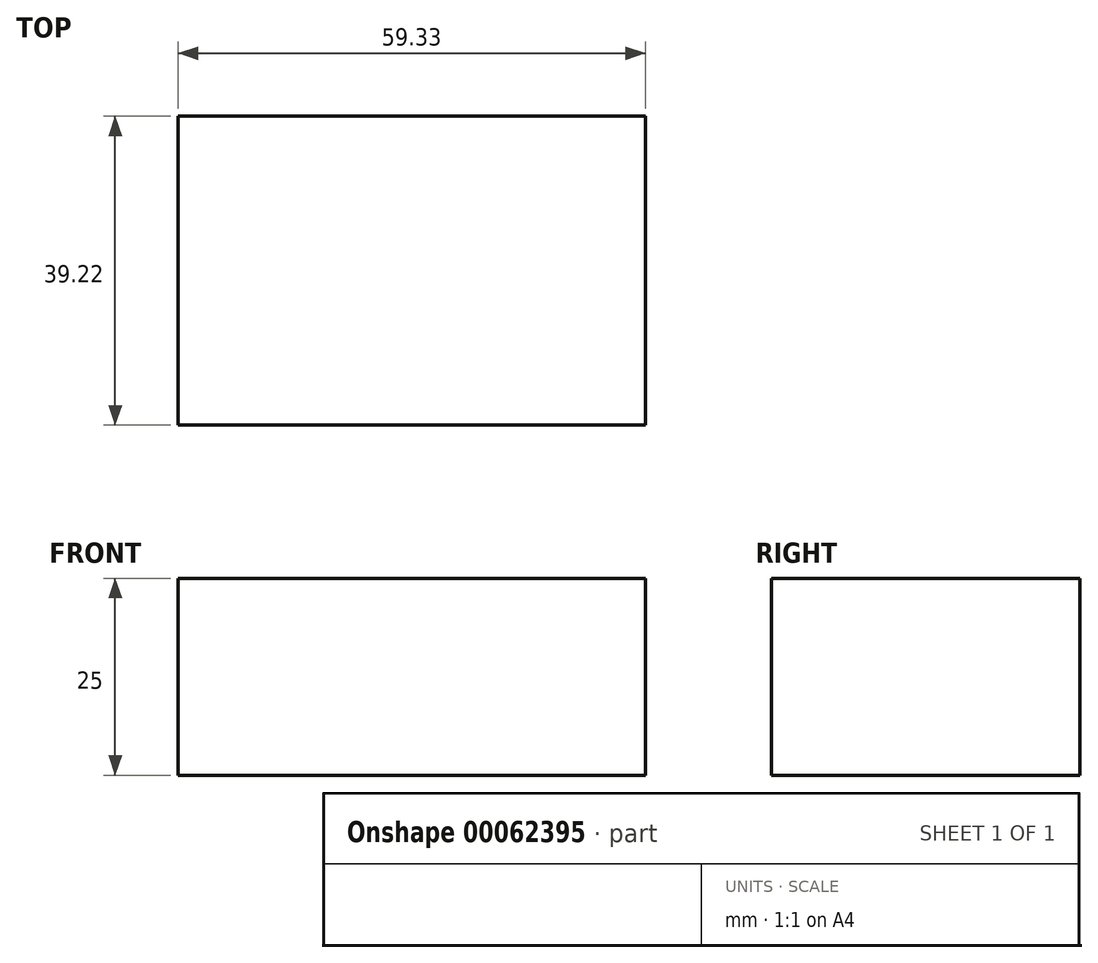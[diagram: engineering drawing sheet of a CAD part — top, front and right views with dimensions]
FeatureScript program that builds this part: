
annotation { "Feature Type Name" : "Feature", "Feature Type Description" : "" }
export const myFeature = defineFeature(function(context is Context, id is Id, definition is map)
    precondition{}
    {
        {
            var Q0;
            Q0=qCreatedBy(makeId("Top.planeOp"),FACE);
            var sketch = newSketch(context, id + "F0", { "sketchPlane" : qUnion([Q0])});
            skLineSegment(sketch, "E0.bottom", {"start": v(0, 0) * mm, "end": v(59.33, 0) * mm});
            skLineSegment(sketch, "E0.top", {"start": v(0, 39.22) * mm, "end": v(59.33, 39.22) * mm});
            skLineSegment(sketch, "E0.left", {"start": v(0, 0) * mm, "end": v(0, 39.22) * mm});
            skLineSegment(sketch, "E0.right", {"start": v(59.33, 0) * mm, "end": v(59.33, 39.22) * mm});
            skSolve(sketch);
        }
        {
            var Q0;
            Q0=makeQuery(id+"F0.imprint","IMPRINT",FACE,{"disambiguationData":[TD([[makeQuery(id+"F0.imprint","IMPRINT",EDGE,{"derivedFrom":sQuery(id+"F0.wireOp",EDGE,"E0.bottom")}),1.0]])]});
            extrude(context, id + "F1", {"entities" : qUnion([Q0]), "depth" : 25 * mm});
        }
    });
